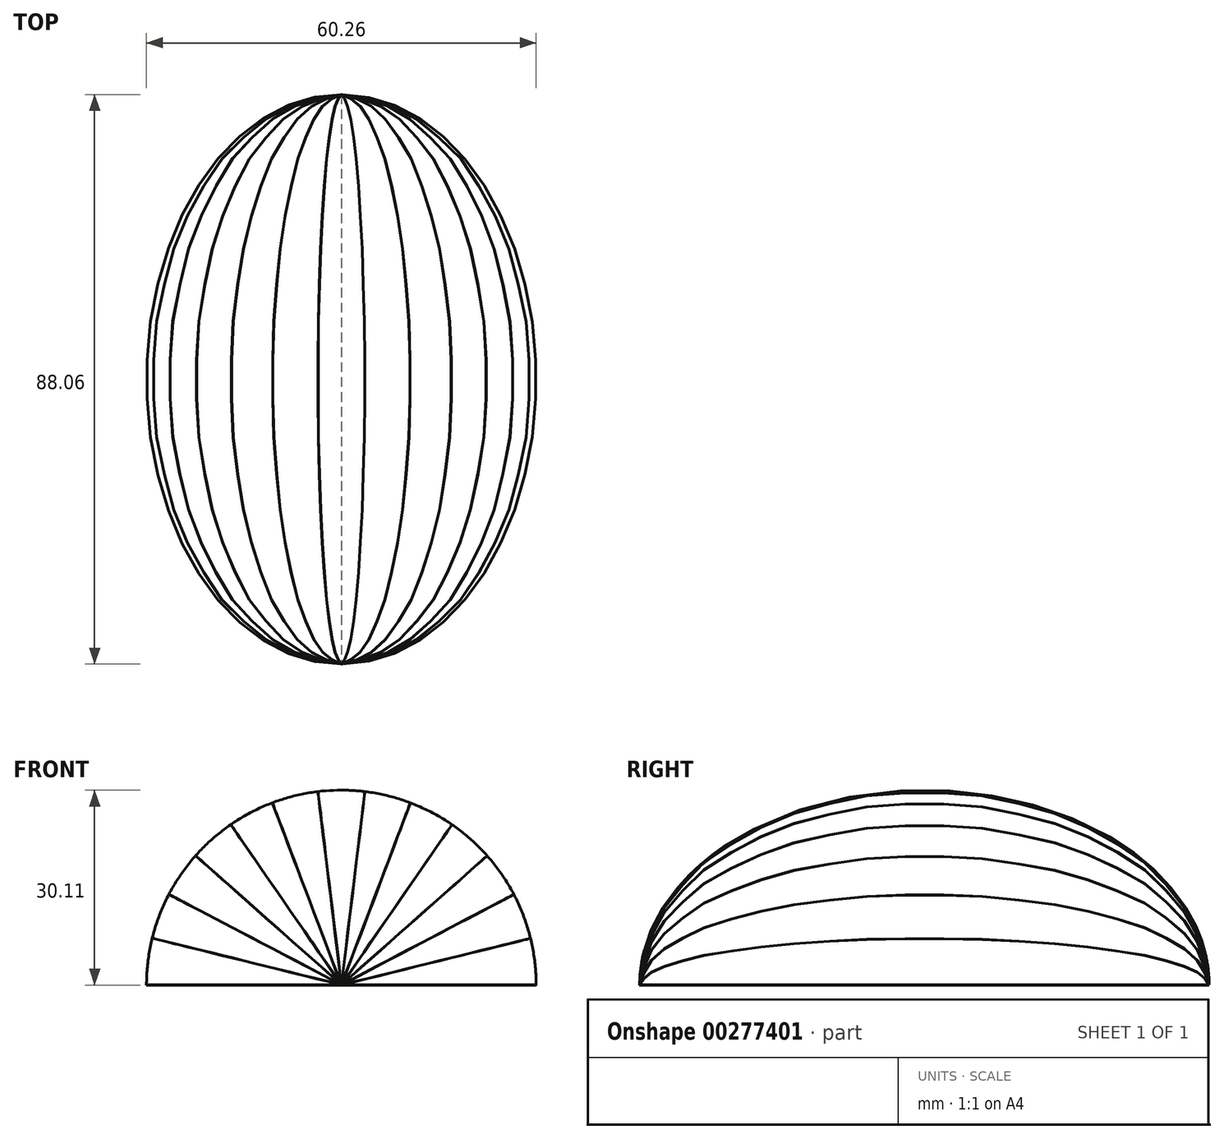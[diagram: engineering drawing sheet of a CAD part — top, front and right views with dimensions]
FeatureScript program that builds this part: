
annotation { "Feature Type Name" : "Feature", "Feature Type Description" : "" }
export const myFeature = defineFeature(function(context is Context, id is Id, definition is map)
    precondition{}
    {
        {
            var Q0;
            Q0=qCreatedBy(makeId("Top.planeOp"),FACE);
            var sketch = newSketch(context, id + "F0", { "sketchPlane" : qUnion([Q0])});
            skEllipticalArc(sketch, "E0", {});
            skLineSegment(sketch, "E1", {"start": v(0, 44.03) * mm, "end": v(0, -44.03) * mm});
            const initialGuessF0  = {"E0": [0, 0, 0, -1, 0.04402916878461838, 0.030129059883306983, 0, 3.141592653589793]};
            skSetInitialGuess(sketch, initialGuessF0);
            skSolve(sketch);
        }
        {
            var Q0;
            Q0 = qSketchRegion(id + "F0", true);
            var Q1;
            Q1=sQuery(id+"F0.wireOp",EDGE,"E1");
            revolve(context, id + "F1", {"entities" : qUnion([Q0]), "axis" : qUnion([Q1]), "revolveType" : RevolveType.ONE_DIRECTION, "angle" : 180 * degree});
        }
        {
            var Q0;
            Q0=makeQuery(id+"F0.imprint","IMPRINT",FACE,{"disambiguationData":[TD([[makeQuery(id+"F0.imprint","IMPRINT",EDGE,{"derivedFrom":sQuery(id+"F0.wireOp",EDGE,"E0")}),1.0]])]});
            extrude(context, id + "F2", {"entities" : qUnion([Q0]), "depth" : 0.03 * mm});
        }
        {
            var Q0;
            Q0=makeQuery(id+"F2.opExtrude","SWEPT_BODY",BODY,{"disambiguationData":[OSD([sQuery(id+"F0.wireOp",EDGE,"E0"),sQuery(id+"F0.wireOp",EDGE,"E1")])]});
            var Q1;
            Q1=makeQuery(id+"F2.opExtrude","CAP_EDGE",EDGE,{"disambiguationData":[OSD([sQuery(id+"F0.wireOp",EDGE,"E1")])],"isStart":false});
            circularPattern(context, id + "F3", {"entities" : qUnion([Q0]), "axis" : qUnion([Q1]), "angle" : 180 * degree, "instanceCount" : 14, "equalSpace" : true});
        }
    });
